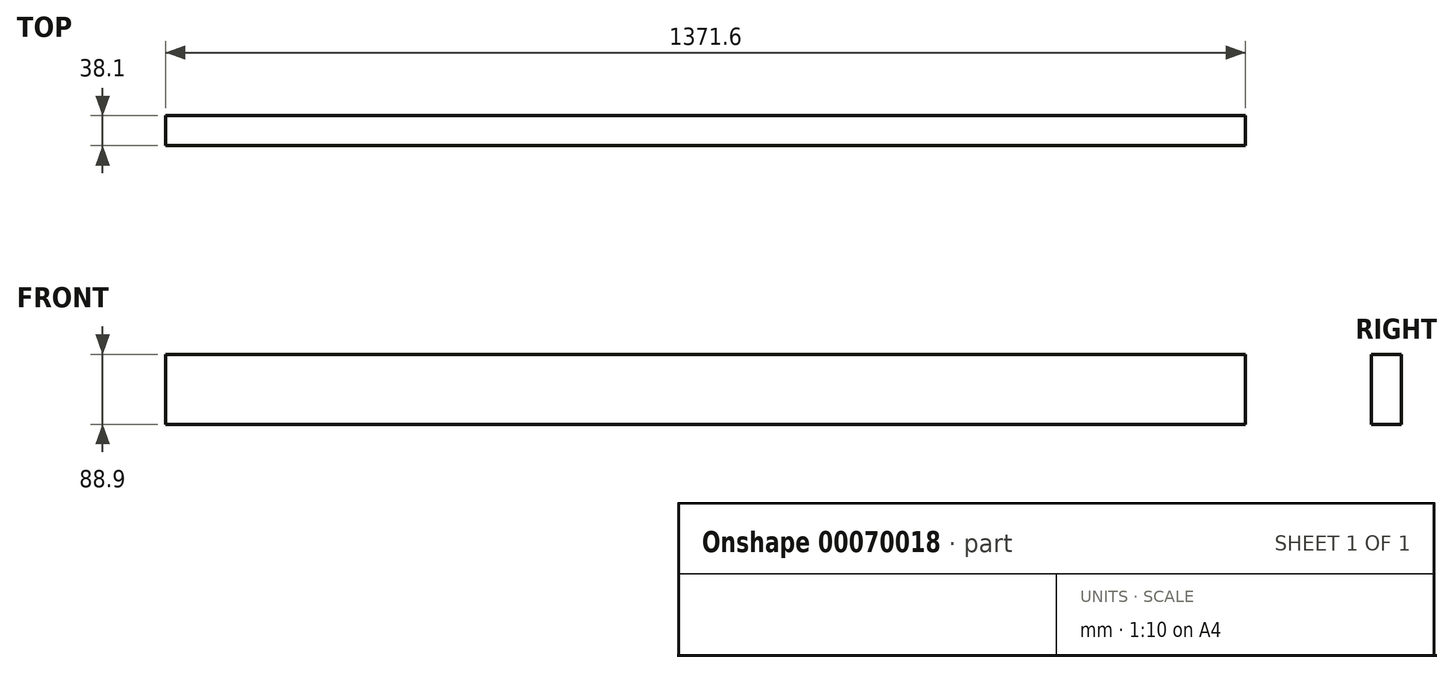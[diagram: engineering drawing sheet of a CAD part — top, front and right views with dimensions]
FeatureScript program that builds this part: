
annotation { "Feature Type Name" : "Feature", "Feature Type Description" : "" }
export const myFeature = defineFeature(function(context is Context, id is Id, definition is map)
    precondition{}
    {
        {
            var Q0;
            Q0=qCreatedBy(makeId("Top.planeOp"),FACE);
            var sketch = newSketch(context, id + "F0", { "sketchPlane" : qUnion([Q0])});
            skLineSegment(sketch, "E0.bottom", {"start": v(0, 0) * mm, "end": v(1371.6, 0) * mm});
            skLineSegment(sketch, "E0.top", {"start": v(0, 38.1) * mm, "end": v(1371.6, 38.1) * mm});
            skLineSegment(sketch, "E0.left", {"start": v(0, 0) * mm, "end": v(0, 38.1) * mm});
            skLineSegment(sketch, "E0.right", {"start": v(1371.6, 0) * mm, "end": v(1371.6, 38.1) * mm});
            skSolve(sketch);
        }
        {
            var Q0;
            Q0=makeQuery(id+"F0.imprint","IMPRINT",FACE,{"disambiguationData":[TD([[makeQuery(id+"F0.imprint","IMPRINT",EDGE,{"derivedFrom":sQuery(id+"F0.wireOp",EDGE,"E0.bottom")}),1.0]])]});
            extrude(context, id + "F1", {"entities" : qUnion([Q0]), "depth" : 88.9 * mm});
        }
    });
